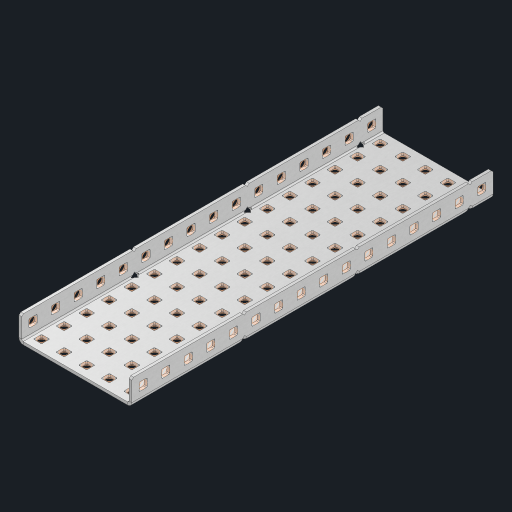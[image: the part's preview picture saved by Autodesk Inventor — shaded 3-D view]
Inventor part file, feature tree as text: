
AUTODESK INVENTOR PART (.ipt)
format: ipt  version: 2023 (Build 270158000, 158)  size: 1,427,456 bytes
history: native  units: in
note: dims shown in document units (in); Inventor stores cm internally (conversion verified against a paired STEP export)
features: other x117, extrude x111, sheet_metal_op x10, sketch x8, mirror x1, pattern_linear x1, chamfer x1
ambient origin geometry x8: Origin, YZ Plane, XZ Plane, XY Plane, X Axis, Y Axis, Z Axis, Center Point
bodies: Solid1 (feature_tree), Body (feature_tree)
feature tree (249):
  other  "Flange Pattern Plane"
  sheet_metal_op  "Flange Pattern"
  sheet_metal_op  "Body Pattern"
  other  "Arc Length"
  mirror  "Notch Mirror"
  pattern_linear  "Notch Pattern"  Spacing1=0.25in  [1 undecoded]
  chamfer  "End Chamfer"
  extrude  "Half Cut"  Depth=0.0625in
  sketch  "Sketch1"  dims[d0=2.5in]
  other  "Plate1"
  sketch  "Sketch2"  dims[d1=8.0in]
  other  "Plate2"
  sheet_metal_op  "Bend1"
  sheet_metal_op  "Corner1"
  sketch  "Sketch3"  dims[d2=0.0625in]
  other  "Flange Pattern Sketch"
  sketch  "Sketch7"  dims[d3=0.0625in]
  other  "Srf1"
  other  "Srf2"
  sketch  "Sketch8"  dims[d4=0.0312in]
  sketch  "Sketch9"  dims[d5=0.125in]
  other  "Srf91"
  sheet_metal_op  "Body Pattern Sketch"
  other  "Srf92"
  sketch  "Sketch13"  dims[d6=0.0625in]
  sketch  "Sketch14"  dims[d7=0.5in d8=90.0deg d9=0.0312in d10=0.25in d11=0.0625in d12=0.0625in d16=0.182in d17=0.02in d18=0.0625in d19=0.0in d20=0.25in d21=0.25in d46=0.172in d47=1.0in d48=0.0in d49=0.182in d50=0.02in d51=0.25in d52=0.25in d53=0.0625in d54=0.0in d55=0.172in d56=1.0in d57=0.0in d60=6.2992in d62=0.5in d63=1.9685in d65=0.5in d85=0.1473in d86=0.1782in d88=0.04in d89=0.0625in d90=0.0in d91=0.04in d92=0.0491in d95=2.5in d96=0.04in d97=0.25in d98=45.0deg d101=0.0in d102=2.497in d131=2.5in d132=6.2992in d134=0.5in d139=0.5in]
  other  "Srf856"
  other  "Srf1310"
  other  "Srf1311"
  other  "Srf1312"
  other  "Srf1376"
  other  "Srf1377"
  other  "Srf1728"
  other  "Srf1755"
  other  "Srf1878"
  other  "Srf1879"
  other  "Srf1880"
  other  "Srf1881"
  other  "Srf1882"
  other  "Srf1883"
  other  "Srf1884"
  other  "Srf1885"
  other  "Srf1886"
  other  "Srf1887"
  other  "Srf1888"
  other  "Srf1889"
  other  "Srf1890"
  other  "Srf1891"
  other  "Srf1892"
  other  "Srf1893"
  other  "Srf1894"
  other  "Srf1895"
  other  "Srf1896"
  other  "Srf1897"
  other  "Srf1898"
  other  "Srf1899"
  other  "Srf1900"
  other  "Srf1901"
  other  "Srf1902"
  other  "Srf1903"
  other  "Srf1942"
  other  "Srf1943"
  other  "Srf1944"
  other  "Srf1945"
  other  "Srf1946"
  other  "Srf1947"
  other  "Srf1948"
  other  "Srf1949"
  other  "Srf1950"
  other  "Srf1951"
  other  "Srf1952"
  other  "Srf1953"
  other  "Srf1954"
  other  "Srf1955"
  other  "Srf1956"
  other  "Srf1957"
  other  "Srf1958"
  other  "Srf1959"
  other  "Srf1960"
  other  "Srf1961"
  other  "Srf1962"
  other  "Srf1963"
  other  "Srf1964"
  other  "Srf1965"
  other  "Srf1966"
  other  "Srf1967"
  other  "Srf1968"
  other  "Srf1969"
  other  "Srf1970"
  other  "Srf2146"
  other  "Srf2147"
  other  "Srf2148"
  other  "Srf2149"
  other  "Srf2150"
  other  "Srf2151"
  other  "Srf2152"
  other  "Srf2153"
  other  "Srf2154"
  other  "Srf2155"
  other  "Srf2156"
  other  "Srf2157"
  other  "Srf2158"
  other  "Srf2159"
  other  "Srf2160"
  other  "Srf2161"
  other  "Srf2162"
  other  "Srf2163"
  other  "Srf2164"
  other  "Srf2165"
  other  "Srf2166"
  other  "Srf2167"
  other  "Srf2168"
  other  "Srf2169"
  other  "Srf2170"
  other  "Srf2171"
  other  "Srf2172"
  other  "Srf2173"
  other  "Srf2174"
  other  "Srf2175"
  other  "Srf2176"
  other  "Srf2177"
  other  "Srf2178"
  other  "Srf2179"
  other  "Srf2180"
  other  "Srf2181"
  other  "Srf2182"
  other  "Srf2183"
  other  "Srf2184"
  other  "Srf2185"
  other  "Srf2186"
  other  "Srf2187"
  other  "Srf2188"
  other  "Srf2189"
  other  "Srf2190"
  sheet_metal_op  "Flange Stamp"
  sheet_metal_op  "Flange Circle"
  sheet_metal_op  "Body Stamp"
  sheet_metal_op  "Body Circle"
  sheet_metal_op  "Notch"
  extrude  "ExtrusionSrf2"  Depth=0.0625in
  extrude  "ExtrusionSrf92"  Depth=2.5in
  extrude  "ExtrusionSrf856"  Depth=0.02in
  extrude  "ExtrusionSrf1310"  Depth=0.0625in
  extrude  "ExtrusionSrf1311"  TaperAngle=0.0deg  [1 undecoded]
  extrude  "ExtrusionSrf1312"  Depth=0.25in
  extrude  "ExtrusionSrf1376"  Depth=0.25in
  extrude  "ExtrusionSrf1377"  Depth=2.5in
  extrude  "ExtrusionSrf1728"  Depth=2.5in TaperAngle=0.0deg
  extrude  "ExtrusionSrf1755"  Depth=2.5in
  extrude  "ExtrusionSrf1878"  Depth=0.02in
  extrude  "ExtrusionSrf1879"  Depth=0.25in
  extrude  "ExtrusionSrf1880"  Depth=0.25in
  extrude  "ExtrusionSrf1881"  Depth=0.0625in
  extrude  "ExtrusionSrf1882"  TaperAngle=0.0deg  [1 undecoded]
  extrude  "ExtrusionSrf1883"  Depth=2.5in
  extrude  "ExtrusionSrf1884"  Depth=2.5in TaperAngle=0.0deg
  extrude  "ExtrusionSrf1885"  Depth=2.5in
  extrude  "ExtrusionSrf1886"  Depth=2.5in
  extrude  "ExtrusionSrf1887"  Depth=2.5in
  extrude  "ExtrusionSrf1888"  Depth=2.5in
  extrude  "ExtrusionSrf1889"  Depth=2.5in
  extrude  "ExtrusionSrf1890"  Depth=0.0625in
  extrude  "ExtrusionSrf1891"  TaperAngle=0.0deg  [1 undecoded]
  extrude  "ExtrusionSrf1892"  Depth=2.5in
  extrude  "ExtrusionSrf1893"  Depth=2.5in
  extrude  "ExtrusionSrf1894"  Depth=2.5in
  extrude  "ExtrusionSrf1895"  Depth=0.25in TaperAngle=45.0deg
  extrude  "ExtrusionSrf1896"  TaperAngle=0.0deg  [1 undecoded]
  extrude  "ExtrusionSrf1897"  Depth=2.5in
  extrude  "ExtrusionSrf1898"  Depth=2.5in
  extrude  "ExtrusionSrf1899"  Depth=2.5in
  extrude  "ExtrusionSrf1900"  Depth=2.5in
  extrude  "ExtrusionSrf1901"  Depth=2.5in
  extrude  "ExtrusionSrf1902"  [1 undecoded]
  extrude  "ExtrusionSrf1903"  [1 undecoded]
  extrude  "ExtrusionSrf1942"  [1 undecoded]
  extrude  "ExtrusionSrf1943"  [1 undecoded]
  extrude  "ExtrusionSrf1944"  [1 undecoded]
  extrude  "ExtrusionSrf1945"  [1 undecoded]
  extrude  "ExtrusionSrf1946"  [1 undecoded]
  extrude  "ExtrusionSrf1947"  [1 undecoded]
  extrude  "ExtrusionSrf1948"  [1 undecoded]
  extrude  "ExtrusionSrf1949"  [1 undecoded]
  extrude  "ExtrusionSrf1950"  [1 undecoded]
  extrude  "ExtrusionSrf1951"  [1 undecoded]
  extrude  "ExtrusionSrf1952"  [1 undecoded]
  extrude  "ExtrusionSrf1953"  [1 undecoded]
  extrude  "ExtrusionSrf1954"  [1 undecoded]
  extrude  "ExtrusionSrf1955"  [1 undecoded]
  extrude  "ExtrusionSrf1956"  [1 undecoded]
  extrude  "ExtrusionSrf1957"  [1 undecoded]
  extrude  "ExtrusionSrf1958"  [1 undecoded]
  extrude  "ExtrusionSrf1959"  [1 undecoded]
  extrude  "ExtrusionSrf1960"  [1 undecoded]
  extrude  "ExtrusionSrf1961"  [1 undecoded]
  extrude  "ExtrusionSrf1962"  [1 undecoded]
  extrude  "ExtrusionSrf1963"  [1 undecoded]
  extrude  "ExtrusionSrf1964"  [1 undecoded]
  extrude  "ExtrusionSrf1965"  [1 undecoded]
  extrude  "ExtrusionSrf1966"  [1 undecoded]
  extrude  "ExtrusionSrf1967"  [1 undecoded]
  extrude  "ExtrusionSrf1968"  [1 undecoded]
  extrude  "ExtrusionSrf1969"  [1 undecoded]
  extrude  "ExtrusionSrf1970"  [1 undecoded]
  extrude  "ExtrusionSrf2146"  [1 undecoded]
  extrude  "ExtrusionSrf2147"  [1 undecoded]
  extrude  "ExtrusionSrf2148"  [1 undecoded]
  extrude  "ExtrusionSrf2149"  [1 undecoded]
  extrude  "ExtrusionSrf2150"  [1 undecoded]
  extrude  "ExtrusionSrf2151"  [1 undecoded]
  extrude  "ExtrusionSrf2152"  [1 undecoded]
  extrude  "ExtrusionSrf2153"  [1 undecoded]
  extrude  "ExtrusionSrf2154"  [1 undecoded]
  extrude  "ExtrusionSrf2155"  [1 undecoded]
  extrude  "ExtrusionSrf2156"  [1 undecoded]
  extrude  "ExtrusionSrf2157"  [1 undecoded]
  extrude  "ExtrusionSrf2158"  [1 undecoded]
  extrude  "ExtrusionSrf2159"  [1 undecoded]
  extrude  "ExtrusionSrf2160"  [1 undecoded]
  extrude  "ExtrusionSrf2161"  [1 undecoded]
  extrude  "ExtrusionSrf2162"  [1 undecoded]
  extrude  "ExtrusionSrf2163"  [1 undecoded]
  extrude  "ExtrusionSrf2164"  [1 undecoded]
  extrude  "ExtrusionSrf2165"  [1 undecoded]
  extrude  "ExtrusionSrf2166"  [1 undecoded]
  extrude  "ExtrusionSrf2167"  [1 undecoded]
  extrude  "ExtrusionSrf2168"  [1 undecoded]
  extrude  "ExtrusionSrf2169"  [1 undecoded]
  extrude  "ExtrusionSrf2170"  [1 undecoded]
  extrude  "ExtrusionSrf2171"  [1 undecoded]
  extrude  "ExtrusionSrf2172"  [1 undecoded]
  extrude  "ExtrusionSrf2173"  [1 undecoded]
  extrude  "ExtrusionSrf2174"  [1 undecoded]
  extrude  "ExtrusionSrf2175"  [1 undecoded]
  extrude  "ExtrusionSrf2176"  [1 undecoded]
  extrude  "ExtrusionSrf2177"  [1 undecoded]
  extrude  "ExtrusionSrf2178"  [1 undecoded]
  extrude  "ExtrusionSrf2179"  [1 undecoded]
  extrude  "ExtrusionSrf2180"  [1 undecoded]
  extrude  "ExtrusionSrf2181"  [1 undecoded]
  extrude  "ExtrusionSrf2182"  [1 undecoded]
  extrude  "ExtrusionSrf2183"  [1 undecoded]
  extrude  "ExtrusionSrf2184"  [1 undecoded]
  extrude  "ExtrusionSrf2185"  [1 undecoded]
  extrude  "ExtrusionSrf2186"  [1 undecoded]
  extrude  "ExtrusionSrf2187"  [1 undecoded]
  extrude  "ExtrusionSrf2188"  [1 undecoded]
  extrude  "ExtrusionSrf2189"  [1 undecoded]
  extrude  "ExtrusionSrf2190"  [1 undecoded]
note: 81 required parameter values undecoded (feature->parameter linkage not recoverable at this tier; creation-order binding heuristic only, values carry confidence <= 0.55)
